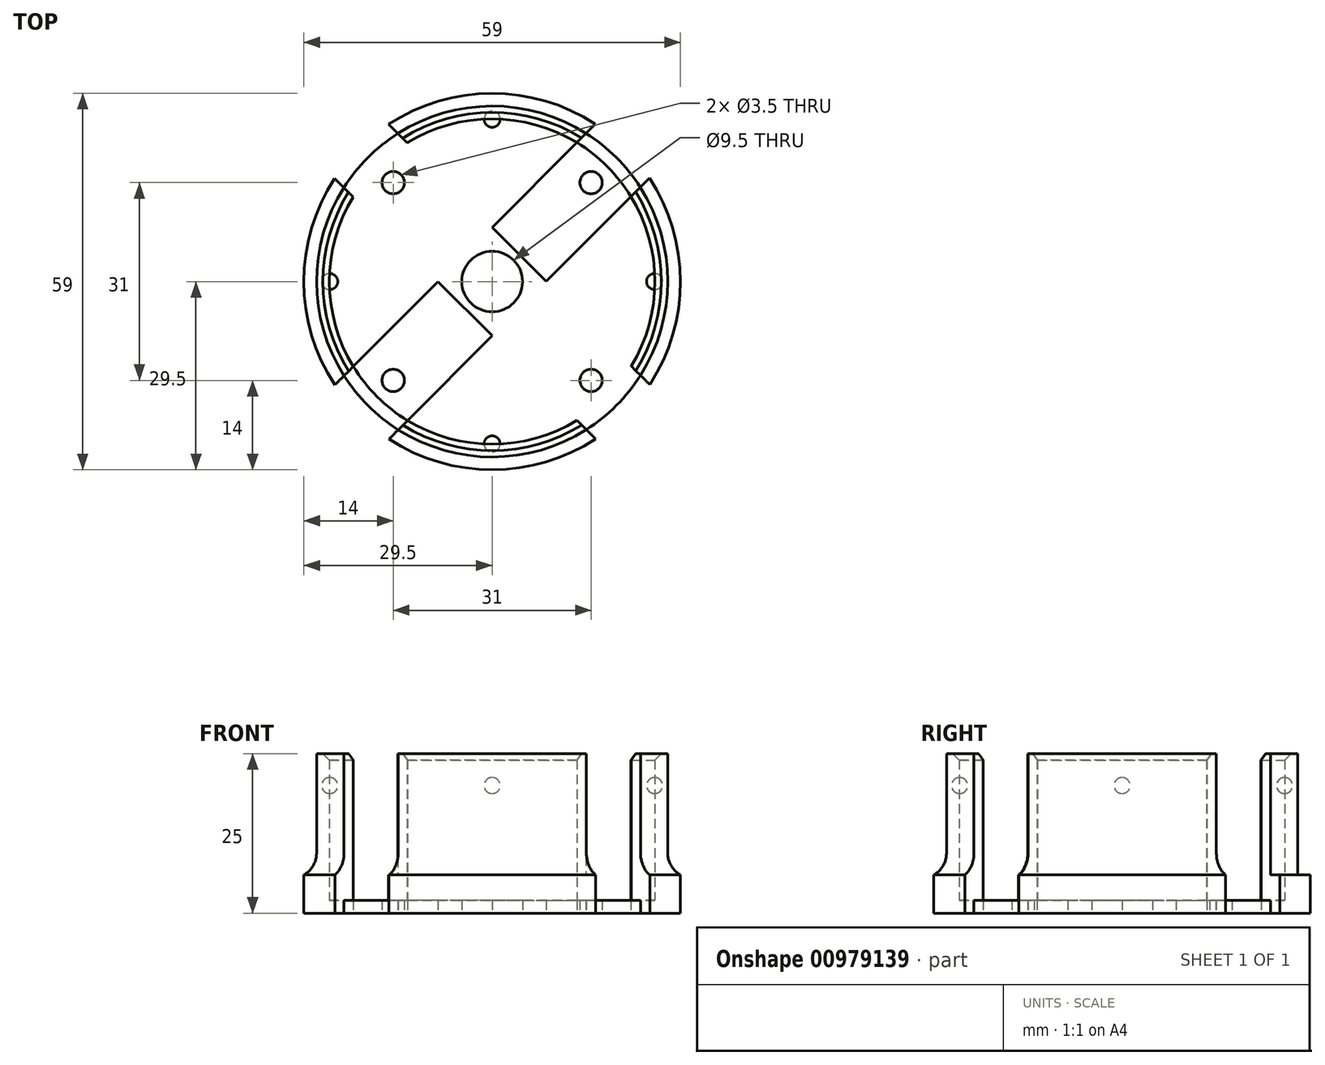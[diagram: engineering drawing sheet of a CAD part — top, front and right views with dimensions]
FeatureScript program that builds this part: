
annotation { "Feature Type Name" : "Feature", "Feature Type Description" : "" }
export const myFeature = defineFeature(function(context is Context, id is Id, definition is map)
    precondition{}
    {
        {
            var Q0;
            Q0=qCreatedBy(makeId("Top.planeOp"),FACE);
            var sketch = newSketch(context, id + "F0", { "sketchPlane" : qUnion([Q0])});
            skCircle(sketch, "E0", {"center": v(0, 0) * mm, "radius": 25.5 * mm});
            skCircle(sketch, "E1", {"center": v(0, 0) * mm, "radius": 27.5 * mm});
            skLineSegment(sketch, "E2.bottom", {"start": v(15.5, -15.5) * mm, "end": v(-15.5, -15.5) * mm, "construction": true});
            skLineSegment(sketch, "E2.top", {"start": v(15.5, 15.5) * mm, "end": v(-15.5, 15.5) * mm, "construction": true});
            skLineSegment(sketch, "E2.left", {"start": v(15.5, -15.5) * mm, "end": v(15.5, 15.5) * mm, "construction": true});
            skLineSegment(sketch, "E2.right", {"start": v(-15.5, -15.5) * mm, "end": v(-15.5, 15.5) * mm, "construction": true});
            skCircle(sketch, "E3", {"center": v(-15.5, 15.5) * mm, "radius": 1.75 * mm});
            skCircle(sketch, "E4.MirrorC", {"center": v(15.5, 15.5) * mm, "radius": 1.75 * mm});
            skCircle(sketch, "E5.MirrorC", {"center": v(-15.5, -15.5) * mm, "radius": 1.75 * mm});
            skCircle(sketch, "E6.MirrorC", {"center": v(15.5, -15.5) * mm, "radius": 1.75 * mm});
            skLineSegment(sketch, "E7.0", {"start": v(-4.24, -4.25) * mm, "end": v(17.99, -26.42) * mm});
            skLineSegment(sketch, "E8.0", {"start": v(4.24, 4.25) * mm, "end": v(26.46, -17.92) * mm});
            skLineSegment(sketch, "E9", {"start": v(17.99, -26.42) * mm, "end": v(26.46, -17.92) * mm});
            skLineSegment(sketch, "E10.1.1", {"start": v(4.25, -4.24) * mm, "end": v(26.42, 17.99) * mm});
            skLineSegment(sketch, "E10.1.2", {"start": v(-4.25, 4.24) * mm, "end": v(17.92, 26.46) * mm});
            skLineSegment(sketch, "E10.1.3", {"start": v(26.42, 17.99) * mm, "end": v(17.92, 26.46) * mm});
            skLineSegment(sketch, "E10.2.1", {"start": v(4.24, 4.25) * mm, "end": v(-17.99, 26.42) * mm});
            skLineSegment(sketch, "E10.2.2", {"start": v(-4.24, -4.25) * mm, "end": v(-26.46, 17.92) * mm});
            skLineSegment(sketch, "E10.2.3", {"start": v(-17.99, 26.42) * mm, "end": v(-26.46, 17.92) * mm});
            skLineSegment(sketch, "E10.3.1", {"start": v(-4.25, 4.24) * mm, "end": v(-26.42, -17.99) * mm});
            skLineSegment(sketch, "E10.3.2", {"start": v(4.25, -4.24) * mm, "end": v(-17.92, -26.46) * mm});
            skLineSegment(sketch, "E10.3.3", {"start": v(-26.42, -17.99) * mm, "end": v(-17.92, -26.46) * mm});
            skCircle(sketch, "E11", {"center": v(0, 0) * mm, "radius": 4.75 * mm});
            skCircle(sketch, "E12", {"center": v(0, 0) * mm, "radius": 29.5 * mm});
            skSolve(sketch);
        }
        {
            var Q0;
            Q0=makeQuery(id+"F0.imprint","IMPRINT",FACE,{"disambiguationData":[TD([[makeQuery(id+"F0.imprint","IMPRINT",EDGE,{"derivedFrom":sQuery(id+"F0.wireOp",EDGE,"E0")}),1.0]])]});
            var Q1;
            Q1=makeQuery(id+"F0.imprint","IMPRINT",FACE,{"disambiguationData":[TD([[makeQuery(id+"F0.imprint","IMPRINT",EDGE,{"derivedFrom":sQuery(id+"F0.wireOp",EDGE,"E6.MirrorC")}),-1.0]])]});
            var Q2;
            Q2=makeQuery(id+"F0.imprint","IMPRINT",FACE,{"disambiguationData":[TD([[makeQuery(id+"F0.imprint","IMPRINT",EDGE,{"derivedFrom":sQuery(id+"F0.wireOp",EDGE,"E4.MirrorC")}),1.0]])]});
            var Q3;
            Q3=makeQuery(id+"F0.imprint","IMPRINT",FACE,{"disambiguationData":[TD([[makeQuery(id+"F0.imprint","IMPRINT",EDGE,{"derivedFrom":sQuery(id+"F0.wireOp",EDGE,"E3")}),-1.0]])]});
            var Q4;
            {var subQ10=sQuery(id+"F0.wireOp",EDGE,"E7.0");var subQ13=sQuery(id+"F0.wireOp",EDGE,"E10.2.2");var subQ14=makeQuery(id+"F0.imprint","INTERSECT",VERTEX,{"derivedFrom":[subQ10,subQ13]});Q4=makeQuery(id+"F0.imprint","IMPRINT",FACE,{"disambiguationData":[TD([[makeQuery(id+"F0.imprint","IMPRINT",EDGE,{"disambiguationData":[TD([[subQ14,-1.0]])],"derivedFrom":subQ10}),1.0]])]});}
            var Q5;
            Q5=makeQuery(id+"F0.imprint","IMPRINT",FACE,{"disambiguationData":[TD([[makeQuery(id+"F0.imprint","IMPRINT",EDGE,{"derivedFrom":sQuery(id+"F0.wireOp",EDGE,"E5.MirrorC")}),1.0]])]});
            extrude(context, id + "F1", {"entities" : qUnion([Q0, Q1, Q2, Q3, Q4, Q5]), "depth" : 2 * mm, "offsetDistance" : 25 * mm});
        }
        {
            var Q0;
            Q0=makeQuery(id+"F0.imprint","IMPRINT",FACE,{"disambiguationData":[TD([[makeQuery(id+"F0.imprint","IMPRINT",EDGE,{"derivedFrom":sQuery(id+"F0.wireOp",EDGE,"E0")}),-1.0]])]});
            extrude(context, id + "F2", {"entities" : qUnion([Q0]), "operationType" : NewBodyOperationType.ADD, "depth" : 25 * mm, "offsetDistance" : 25 * mm});
        }
        {
            var Q0;
            Q0=makeQuery(id+"F2.opExtrude","CAP_EDGE",EDGE,{"disambiguationData":[OSD([sQuery(id+"F0.wireOp",EDGE,"E0")])],"isStart":false});
            chamfer(context, id + "F3", {"entities" : qUnion([Q0]), "width" : 1 * mm, "tangentPropagation" : true});
        }
        {
            var Q0;
            Q0=qCreatedBy(makeId("Right.planeOp"),FACE);
            var sketch = newSketch(context, id + "F4", { "sketchPlane" : qUnion([Q0])});
            skCircle(sketch, "E13", {"center": v(-31.37, 20) * mm, "radius": 1.25 * mm});
            skLineSegment(sketch, "E14", {"start": v(-31.37, 17.2) * mm, "end": v(-31.37, 24.02) * mm});
            skSolve(sketch);
        }
        {
            var Q0;
            {var subQ0=sQuery(id+"F4.wireOp",EDGE,"E14");var subQ1=sQuery(id+"F4.wireOp",EDGE,"E13");var subQ2=makeQuery(id+"F4.imprint","INTERSECT",VERTEX,{"disambiguationData":[OD(0.0)],"derivedFrom":[subQ1,subQ0]});Q0=makeQuery(id+"F4.imprint","IMPRINT",FACE,{"disambiguationData":[TD([[makeQuery(id+"F4.imprint","IMPRINT",EDGE,{"disambiguationData":[TD([[subQ2,-1.0]])],"derivedFrom":subQ1}),1.0]])]});}
            var Q1;
            Q1=sQuery(id+"F4.wireOp",EDGE,"E14");
            revolve(context, id + "F5", {"surfaceOperationType" : NewSurfaceOperationType.NEW, "entities" : qUnion([Q0]), "axis" : qUnion([Q1]), "revolveType" : RevolveType.FULL});
        }
        {
            var Q0;
            Q0=makeQuery(id+"F5.opRevolve","SWEPT_BODY",BODY,{"disambiguationData":[OSD([sQuery(id+"F4.wireOp",EDGE,"E13"),sQuery(id+"F4.wireOp",EDGE,"E14")])]});
            transform(context, id + "F6", {"entities" : qUnion([Q0]), "transformType" : TransformType.TRANSLATION_3D, "dx" : 0 * mm, "dy" : 5.9 * mm, "dz" : 0 * mm, "makeCopy" : false});
        }
        {
            var Q0;
            Q0=makeQuery(id+"F5.opRevolve","SWEPT_BODY",BODY,{"disambiguationData":[OSD([sQuery(id+"F4.wireOp",EDGE,"E13"),sQuery(id+"F4.wireOp",EDGE,"E14")])]});
            transform(context, id + "F7", {"entities" : qUnion([Q0]), "transformType" : TransformType.TRANSLATION_3D, "dx" : 0 * mm, "dy" : 50.9 * mm, "dz" : 0 * mm, "makeCopy" : true});
        }
        {
            var Q0;
            Q0=qCreatedBy(makeId("Right.planeOp"),FACE);
            var sketch = newSketch(context, id + "F8", { "sketchPlane" : qUnion([Q0])});
            skLineSegment(sketch, "E15", {"start": v(0, 0) * mm, "end": v(0, 45.94) * mm});
            skSolve(sketch);
        }
        {
            var Q0;
            Q0=makeQuery(id+"F5.opRevolve","SWEPT_BODY",BODY,{"disambiguationData":[OSD([sQuery(id+"F4.wireOp",EDGE,"E13"),sQuery(id+"F4.wireOp",EDGE,"E14")])]});
            var Q1;
            Q1=makeQuery(id+"F7.opPattern","COPY",BODY,{"derivedFrom":makeQuery(id+"F5.opRevolve","SWEPT_BODY",BODY,{"disambiguationData":[OSD([sQuery(id+"F4.wireOp",EDGE,"E13"),sQuery(id+"F4.wireOp",EDGE,"E14")])]}),"instanceName":"1"});
            var Q2;
            Q2=sQuery(id+"F8.wireOp",EDGE,"E15");
            circularPattern(context, id + "F9", {"entities" : qUnion([Q0, Q1]), "axis" : qUnion([Q2]), "angle" : 360 * degree, "instanceCount" : 4, "equalSpace" : true});
        }
        {
            var Q0;
            {var subQ0=sQuery(id+"F0.wireOp",EDGE,"E10.1.2");var subQ1=sQuery(id+"F0.wireOp",EDGE,"E0");var subQ2=makeQuery(id+"F0.imprint","INTERSECT",VERTEX,{"derivedFrom":[subQ1,subQ0]});Q0=makeQuery(id+"F0.imprint","IMPRINT",FACE,{"disambiguationData":[TD([[makeQuery(id+"F0.imprint","IMPRINT",EDGE,{"disambiguationData":[TD([[subQ2,1.0]])],"derivedFrom":subQ1}),-1.0]])]});}
            var Q1;
            {var subQ0=sQuery(id+"F0.wireOp",EDGE,"E10.2.1");var subQ1=sQuery(id+"F0.wireOp",EDGE,"E0");var subQ2=makeQuery(id+"F0.imprint","INTERSECT",VERTEX,{"derivedFrom":[subQ1,subQ0]});Q1=makeQuery(id+"F0.imprint","IMPRINT",FACE,{"disambiguationData":[TD([[makeQuery(id+"F0.imprint","IMPRINT",EDGE,{"disambiguationData":[TD([[subQ2,-1.0]])],"derivedFrom":subQ1}),-1.0]])]});}
            var Q2;
            {var subQ0=sQuery(id+"F0.wireOp",EDGE,"E10.3.1");var subQ1=sQuery(id+"F0.wireOp",EDGE,"E0");var subQ2=makeQuery(id+"F0.imprint","INTERSECT",VERTEX,{"derivedFrom":[subQ1,subQ0]});Q2=makeQuery(id+"F0.imprint","IMPRINT",FACE,{"disambiguationData":[TD([[makeQuery(id+"F0.imprint","IMPRINT",EDGE,{"disambiguationData":[TD([[subQ2,-1.0]])],"derivedFrom":subQ1}),-1.0]])]});}
            var Q3;
            {var subQ0=sQuery(id+"F0.wireOp",EDGE,"E7.0");var subQ1=sQuery(id+"F0.wireOp",EDGE,"E0");var subQ2=makeQuery(id+"F0.imprint","INTERSECT",VERTEX,{"derivedFrom":[subQ1,subQ0]});Q3=makeQuery(id+"F0.imprint","IMPRINT",FACE,{"disambiguationData":[TD([[makeQuery(id+"F0.imprint","IMPRINT",EDGE,{"disambiguationData":[TD([[subQ2,-1.0]])],"derivedFrom":subQ1}),-1.0]])]});}
            extrude(context, id + "F10", {"entities" : qUnion([Q0, Q1, Q2, Q3]), "operationType" : NewBodyOperationType.REMOVE, "depth" : 25 * mm, "offsetDistance" : 25 * mm, "hasSecondDirection" : true, "secondDirectionOppositeDirection" : false, "secondDirectionDepth" : 2 * mm});
        }
        {
            var Q0;
            {var subQ0=sQuery(id+"F0.wireOp",EDGE,"E10.1.1");var subQ1=sQuery(id+"F0.wireOp",EDGE,"E1");var subQ2=makeQuery(id+"F0.imprint","INTERSECT",VERTEX,{"derivedFrom":[subQ1,subQ0]});Q0=makeQuery(id+"F0.imprint","IMPRINT",FACE,{"disambiguationData":[TD([[makeQuery(id+"F0.imprint","IMPRINT",EDGE,{"disambiguationData":[TD([[subQ2,1.0]])],"derivedFrom":subQ1}),-1.0]])]});}
            var Q1;
            {var subQ0=sQuery(id+"F0.wireOp",EDGE,"E10.1.2");var subQ1=sQuery(id+"F0.wireOp",EDGE,"E1");var subQ2=makeQuery(id+"F0.imprint","INTERSECT",VERTEX,{"derivedFrom":[subQ1,subQ0]});Q1=makeQuery(id+"F0.imprint","IMPRINT",FACE,{"disambiguationData":[TD([[makeQuery(id+"F0.imprint","IMPRINT",EDGE,{"disambiguationData":[TD([[subQ2,-1.0]])],"derivedFrom":subQ1}),-1.0]])]});}
            var Q2;
            {var subQ0=sQuery(id+"F0.wireOp",EDGE,"E10.2.2");var subQ1=sQuery(id+"F0.wireOp",EDGE,"E1");var subQ2=makeQuery(id+"F0.imprint","INTERSECT",VERTEX,{"derivedFrom":[subQ1,subQ0]});Q2=makeQuery(id+"F0.imprint","IMPRINT",FACE,{"disambiguationData":[TD([[makeQuery(id+"F0.imprint","IMPRINT",EDGE,{"disambiguationData":[TD([[subQ2,-1.0]])],"derivedFrom":subQ1}),-1.0]])]});}
            var Q3;
            {var subQ0=sQuery(id+"F0.wireOp",EDGE,"E10.3.2");var subQ1=sQuery(id+"F0.wireOp",EDGE,"E1");var subQ2=makeQuery(id+"F0.imprint","INTERSECT",VERTEX,{"derivedFrom":[subQ1,subQ0]});Q3=makeQuery(id+"F0.imprint","IMPRINT",FACE,{"disambiguationData":[TD([[makeQuery(id+"F0.imprint","IMPRINT",EDGE,{"disambiguationData":[TD([[subQ2,-1.0]])],"derivedFrom":subQ1}),-1.0]])]});}
            extrude(context, id + "F11", {"entities" : qUnion([Q0, Q1, Q2, Q3]), "operationType" : NewBodyOperationType.ADD, "depth" : 6 * mm, "offsetDistance" : 25 * mm});
        }
        {
            var Q0;
            {var subQ0=sQuery(id+"F0.wireOp",EDGE,"E1");Q0=makeQuery(id+"F11.opExtrude","CAP_EDGE",EDGE,{"disambiguationData":[OSD([subQ0]),TDD([makeQuery(id+"F0.imprint","IMPRINT",EDGE,{"disambiguationData":[TD([[makeQuery(id+"F0.imprint","INTERSECT",VERTEX,{"derivedFrom":[subQ0,sQuery(id+"F0.wireOp",EDGE,"E10.1.1")]}),1.0]])],"derivedFrom":subQ0})])],"isStart":false});}
            var Q1;
            {var subQ0=sQuery(id+"F0.wireOp",EDGE,"E1");Q1=makeQuery(id+"F11.opExtrude","CAP_EDGE",EDGE,{"disambiguationData":[OSD([subQ0]),TDD([makeQuery(id+"F0.imprint","IMPRINT",EDGE,{"disambiguationData":[TD([[makeQuery(id+"F0.imprint","INTERSECT",VERTEX,{"derivedFrom":[subQ0,sQuery(id+"F0.wireOp",EDGE,"E10.3.2")]}),-1.0]])],"derivedFrom":subQ0})])],"isStart":false});}
            var Q2;
            {var subQ0=sQuery(id+"F0.wireOp",EDGE,"E1");Q2=makeQuery(id+"F11.opExtrude","CAP_EDGE",EDGE,{"disambiguationData":[OSD([subQ0]),TDD([makeQuery(id+"F0.imprint","IMPRINT",EDGE,{"disambiguationData":[TD([[makeQuery(id+"F0.imprint","INTERSECT",VERTEX,{"derivedFrom":[subQ0,sQuery(id+"F0.wireOp",EDGE,"E10.2.2")]}),-1.0]])],"derivedFrom":subQ0})])],"isStart":false});}
            var Q3;
            {var subQ0=sQuery(id+"F0.wireOp",EDGE,"E1");Q3=makeQuery(id+"F11.opExtrude","CAP_EDGE",EDGE,{"disambiguationData":[OSD([subQ0]),TDD([makeQuery(id+"F0.imprint","IMPRINT",EDGE,{"disambiguationData":[TD([[makeQuery(id+"F0.imprint","INTERSECT",VERTEX,{"derivedFrom":[subQ0,sQuery(id+"F0.wireOp",EDGE,"E10.1.2")]}),-1.0]])],"derivedFrom":subQ0})])],"isStart":false});}
            fillet(context, id + "F12", {"entities" : qUnion([Q0, Q1, Q2, Q3]), "radius" : 4 * mm, "tangentPropagation" : true, "allowEdgeOverflow" : false});
        }
    });
